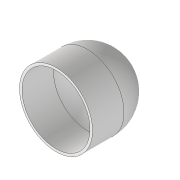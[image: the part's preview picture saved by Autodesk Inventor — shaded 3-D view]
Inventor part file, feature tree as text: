
AUTODESK INVENTOR PART (.ipt)
format: ipt  version: 2020 (Build 240168000, 168)  size: 124,928 bytes
history: native  units: mm
features: revolve x1, sketch x1
ambient origin geometry x8: Origin, YZ Plane, XZ Plane, XY Plane, X Axis, Y Axis, Z Axis, Center Point
bodies: Volumenkörper1 (feature_tree)
feature tree (2):
  revolve  "Umdrehung1"
  sketch  "Skizze1"  dims[d0=3.0mm d1=3.0mm d2=80.0mm d3=80.0mm d4=90.0deg]
